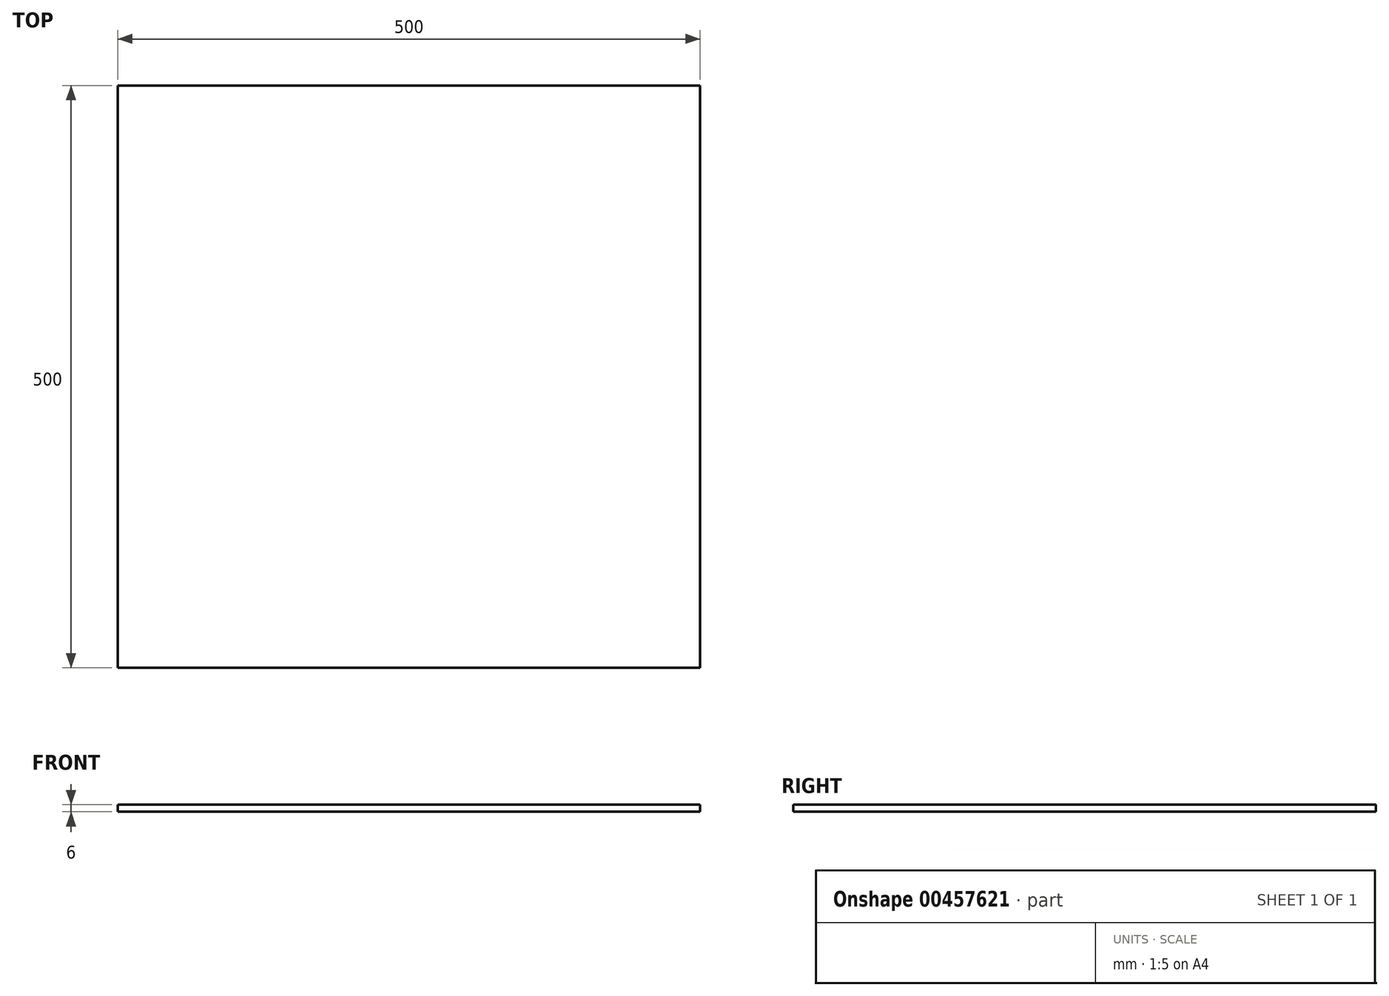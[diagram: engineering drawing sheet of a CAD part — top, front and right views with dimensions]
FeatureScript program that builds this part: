
annotation { "Feature Type Name" : "Feature", "Feature Type Description" : "" }
export const myFeature = defineFeature(function(context is Context, id is Id, definition is map)
    precondition{}
    {
        {
            var Q0;
            Q0=qCreatedBy(makeId("Top.planeOp"),FACE);
            var sketch = newSketch(context, id + "F0", { "sketchPlane" : qUnion([Q0])});
            skLineSegment(sketch, "E0.bottom", {"start": v(250, -250) * mm, "end": v(-250, -250) * mm});
            skLineSegment(sketch, "E0.top", {"start": v(250, 250) * mm, "end": v(-250, 250) * mm});
            skLineSegment(sketch, "E0.left", {"start": v(250, -250) * mm, "end": v(250, 250) * mm});
            skLineSegment(sketch, "E0.right", {"start": v(-250, -250) * mm, "end": v(-250, 250) * mm});
            skPoint(sketch, "E0.middle", {"position": v(0, 0) * mm});
            skSolve(sketch);
        }
        {
            var Q0;
            Q0 = qSketchRegion(id + "F0", true);
            extrude(context, id + "F1", {"entities" : qUnion([Q0]), "depth" : 6 * mm});
        }
    });
